FCSTD DOCUMENT  (FreeCAD 0.14R3702 (Git))
Label: soporte_stand
License: CC-BY 3.0
LicenseURL: http://creativecommons.org/licenses/by/3.0/
objects: Sketcher::SketchObject×1
note: 1 computed .brp shape members not serialized (recipe doc carries the construction recipe); baked Part::Feature solids carry a one-line shape summary decoded from their .brp

FEATURE [Sketcher::SketchObject] Sketch
  sketch-geometry (12):
    g0: LineSegment StartX=0 StartY=0 StartZ=0 EndX=14 EndY=0 EndZ=0
    g1: LineSegment StartX=14 StartY=0 StartZ=0 EndX=14 EndY=6.2 EndZ=0
    g2: LineSegment StartX=14 StartY=6.2 StartZ=0 EndX=30.5 EndY=6.2 EndZ=0
    g3: LineSegment StartX=30.5 StartY=6.2 StartZ=0 EndX=30.5 EndY=0 EndZ=0
    g4: LineSegment StartX=30.5 StartY=0 StartZ=0 EndX=44.5 EndY=0 EndZ=0
    g5: LineSegment StartX=44.5 StartY=0 StartZ=0 EndX=44.5 EndY=8 EndZ=0
    g6: LineSegment StartX=44.5 StartY=8 StartZ=0 EndX=34.5 EndY=8 EndZ=0
    g7: LineSegment StartX=0 StartY=0 StartZ=0 EndX=0 EndY=8 EndZ=0
    g8: LineSegment StartX=0 StartY=8 StartZ=0 EndX=10 EndY=8 EndZ=0
    g9: LineSegment StartX=16.25 StartY=12.2 StartZ=0 EndX=28.25 EndY=12.2 EndZ=0
    g10: LineSegment StartX=10 StartY=8 StartZ=0 EndX=16.25 EndY=12.2 EndZ=0
    g11: LineSegment StartX=28.25 StartY=12.2 StartZ=0 EndX=34.5 EndY=8 EndZ=0
  constraints (35):
    c: Coincident(g-1,g0)
    c: PointOnObject(g0,g-1)
    c: Coincident(g0,g1)
    c: Vertical(g1)
    c: Coincident(g1,g2)
    c: Horizontal(g2)
    c: Coincident(g2,g3)
    c: Vertical(g3)
    c: Coincident(g3,g4)
    c: Horizontal(g4)
    c: Coincident(g4,g5)
    c: Vertical(g5)
    c: Coincident(g5,g6)
    c: Horizontal(g6)
    c: Coincident(g-1,g7)
    c: Vertical(g7)
    c: Coincident(g7,g8)
    c: Horizontal(g8)
    c: Distance(g2) = 16.5
    c: Distance(g0) = 14
    c: Equal(g0,g4)
    c: PointOnObject(g3,g-1)
    c: Distance(g1) = 6.2
    c: Horizontal(g9)
    c: Distance(g9) = 12
    c: Distance(g9,g1) = 2.25
    c: Distance(g2,g9) = 6
    c: Distance(g6) = 10
    c: Equal(g8,g6)
    c: Distance(g7) = 8
    c: Equal(g5,g7)
    c: Coincident(g10,g8)
    c: Coincident(g10,g9)
    c: Coincident(g11,g9)
    c: Coincident(g11,g6)
